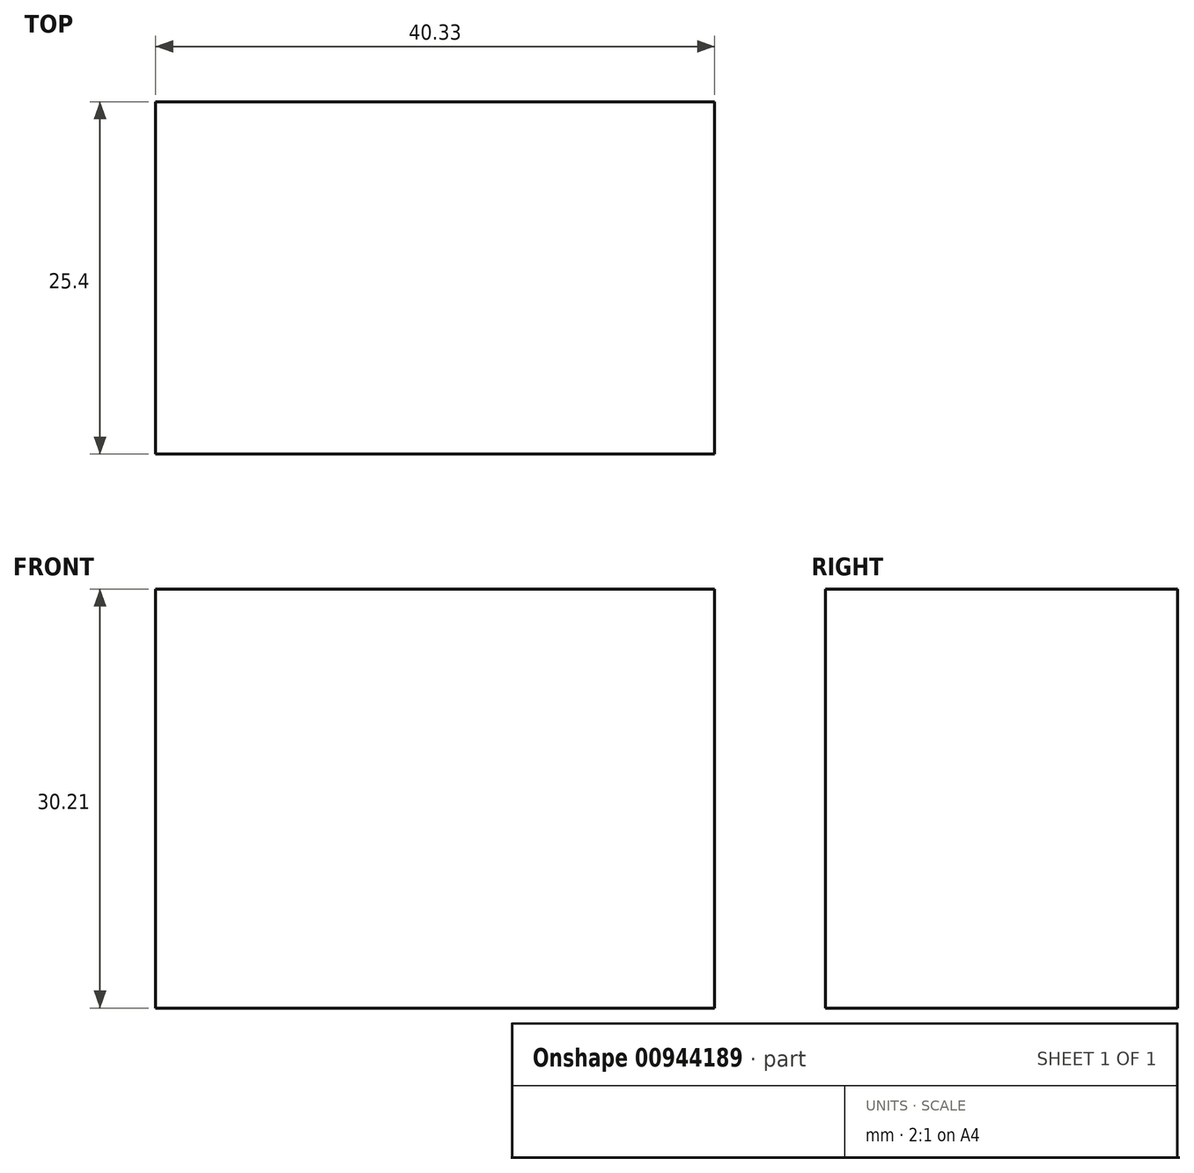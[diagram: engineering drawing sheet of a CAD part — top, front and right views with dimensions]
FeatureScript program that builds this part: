
annotation { "Feature Type Name" : "Feature", "Feature Type Description" : "" }
export const myFeature = defineFeature(function(context is Context, id is Id, definition is map)
    precondition{}
    {
        {
            var Q0;
            Q0=qCreatedBy(makeId("Front.planeOp"),FACE);
            var sketch = newSketch(context, id + "F0", { "sketchPlane" : qUnion([Q0])});
            skLineSegment(sketch, "E0.bottom", {"start": v(-59.34, 26.48) * mm, "end": v(-19, 26.48) * mm});
            skLineSegment(sketch, "E0.top", {"start": v(-59.34, -3.73) * mm, "end": v(-19, -3.73) * mm});
            skLineSegment(sketch, "E0.left", {"start": v(-59.34, 26.48) * mm, "end": v(-59.34, -3.73) * mm});
            skLineSegment(sketch, "E0.right", {"start": v(-19, 26.48) * mm, "end": v(-19, -3.73) * mm});
            skSolve(sketch);
        }
        {
            var Q0;
            Q0 = qSketchRegion(id + "F0", true);
            extrude(context, id + "F1", {"entities" : qUnion([Q0]), "depth" : 25.4 * mm, "offsetDistance" : 25.4 * mm});
        }
    });
